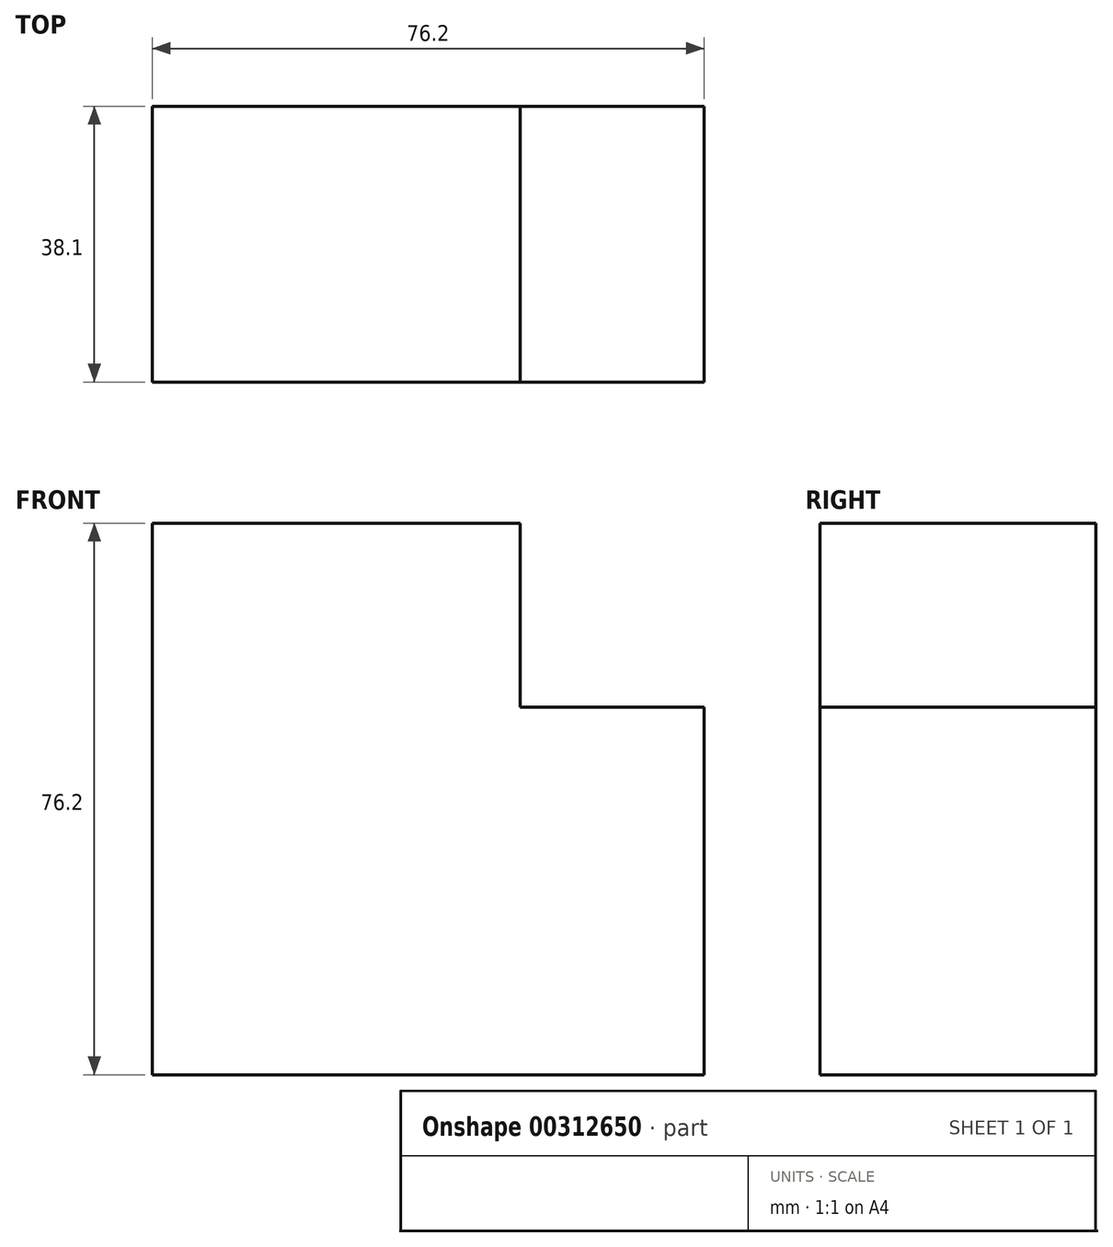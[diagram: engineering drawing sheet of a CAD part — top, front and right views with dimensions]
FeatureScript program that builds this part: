
annotation { "Feature Type Name" : "Feature", "Feature Type Description" : "" }
export const myFeature = defineFeature(function(context is Context, id is Id, definition is map)
    precondition{}
    {
        {
            var Q0;
            Q0=qCreatedBy(makeId("Front.planeOp"),FACE);
            var sketch = newSketch(context, id + "F0", { "sketchPlane" : qUnion([Q0])});
            skLineSegment(sketch, "E0", {"start": v(-61.65, -76.2) * mm, "end": v(14.55, -76.2) * mm});
            skLineSegment(sketch, "E1", {"start": v(14.55, -76.2) * mm, "end": v(14.55, -25.4) * mm});
            skLineSegment(sketch, "E2", {"start": v(14.55, -25.4) * mm, "end": v(-10.85, -25.4) * mm});
            skLineSegment(sketch, "E3", {"start": v(-10.85, 0) * mm, "end": v(-10.85, -25.4) * mm});
            skLineSegment(sketch, "E4", {"start": v(-10.85, 0) * mm, "end": v(-61.65, 0) * mm});
            skLineSegment(sketch, "E5", {"start": v(-61.65, 0) * mm, "end": v(-61.65, -76.2) * mm});
            skSolve(sketch);
        }
        {
            var Q0;
            Q0=makeQuery(id+"F0.imprint","IMPRINT",FACE,{"disambiguationData":[TD([[makeQuery(id+"F0.imprint","IMPRINT",EDGE,{"derivedFrom":sQuery(id+"F0.wireOp",EDGE,"E0")}),1.0]])]});
            extrude(context, id + "F1", {"entities" : qUnion([Q0]), "depth" : 38.1 * mm});
        }
    });
